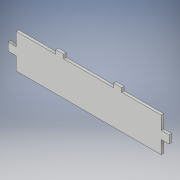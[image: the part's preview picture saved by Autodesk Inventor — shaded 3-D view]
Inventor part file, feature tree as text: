
AUTODESK INVENTOR PART (.ipt)
format: ipt  version: 2018 (Build 220112000, 112)  size: 117,760 bytes
history: native  units: in
note: dims shown in document units (in); Inventor stores cm internally (conversion verified against a paired STEP export)
features: extrude x1, sketch x1
ambient origin geometry x8: Origin, YZ Plane, XZ Plane, XY Plane, X Axis, Y Axis, Z Axis, Center Point
bodies: Solid1 (feature_tree)
feature tree (2):
  extrude  "Extrusion1"  Depth=0.3in
  sketch  "Sketch1"  dims[d0=5.5in d1=0.3in d2=0.15in d3=0.3in d4=0.15in d5=1.5in d6=1.5in d8=1.3in d9=0.3in d10=0.3in d11=0.5in d12=0.3in d13=0.3in d14=0.5in d15=0.1in d16=0.0in]
